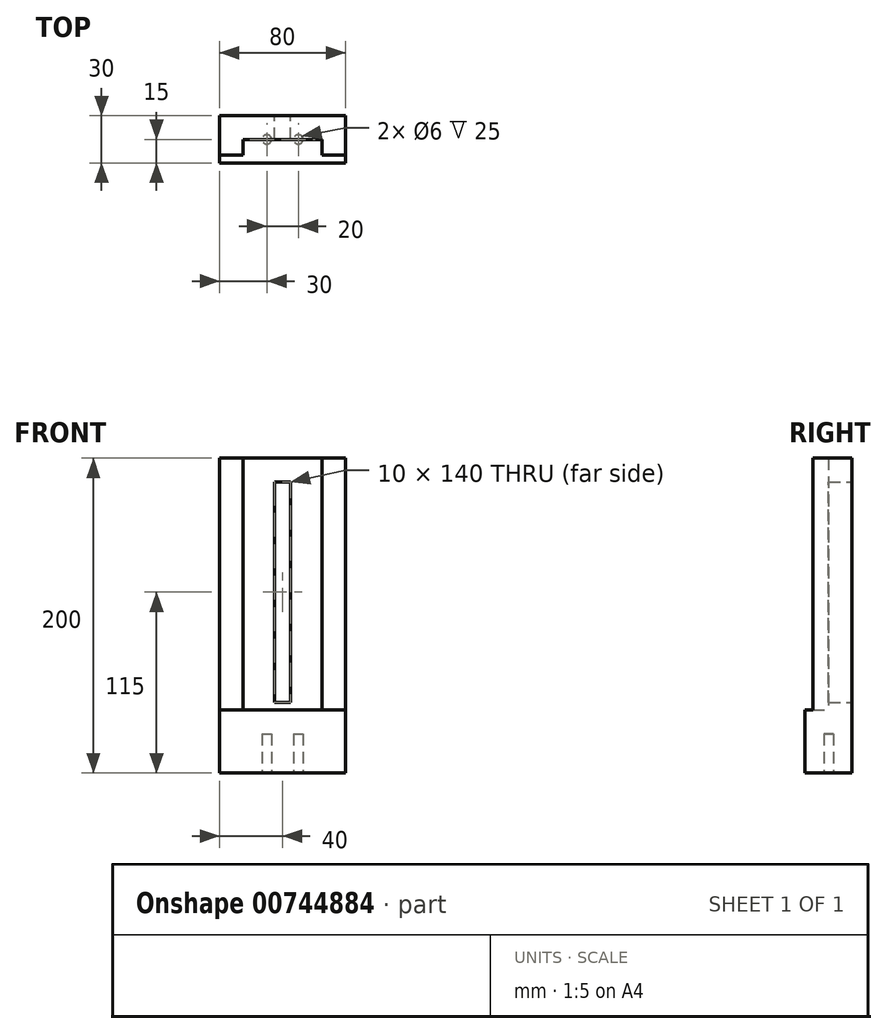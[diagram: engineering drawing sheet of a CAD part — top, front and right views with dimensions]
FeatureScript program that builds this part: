
annotation { "Feature Type Name" : "Feature", "Feature Type Description" : "" }
export const myFeature = defineFeature(function(context is Context, id is Id, definition is map)
    precondition{}
    {
        {
            var Q0;
            Q0=qCreatedBy(makeId("Front.planeOp"),FACE);
            var sketch = newSketch(context, id + "F0", { "sketchPlane" : qUnion([Q0])});
            skLineSegment(sketch, "E0.bottom", {"start": v(40, -100) * mm, "end": v(-40, -100) * mm});
            skLineSegment(sketch, "E0.top", {"start": v(40, 100) * mm, "end": v(-40, 100) * mm});
            skLineSegment(sketch, "E0.left", {"start": v(40, -100) * mm, "end": v(40, 100) * mm});
            skLineSegment(sketch, "E0.right", {"start": v(-40, -100) * mm, "end": v(-40, 100) * mm});
            skPoint(sketch, "E0.middle", {"position": v(0, 0) * mm});
            skLineSegment(sketch, "E1", {"start": v(-40, -60) * mm, "end": v(40, -60) * mm});
            skLineSegment(sketch, "E2", {"start": v(-25, 100) * mm, "end": v(-25, -60) * mm});
            skLineSegment(sketch, "E3.MirrorCS", {"start": v(25, 100) * mm, "end": v(25, -60) * mm});
            skLineSegment(sketch, "E4.bottom", {"start": v(5, -55) * mm, "end": v(-5, -55) * mm});
            skLineSegment(sketch, "E4.top", {"start": v(5, 85) * mm, "end": v(-5, 85) * mm});
            skLineSegment(sketch, "E4.left", {"start": v(5, -55) * mm, "end": v(5, 85) * mm});
            skLineSegment(sketch, "E4.right", {"start": v(-5, -55) * mm, "end": v(-5, 85) * mm});
            skPoint(sketch, "E4.middle", {"position": v(0, 15) * mm});
            skSolve(sketch);
        }
        {
            var Q0;
            {var subQ0=sQuery(id+"F0.wireOp",EDGE,"E2");Q0=makeQuery(id+"F0.imprint","IMPRINT",FACE,{"disambiguationData":[TD([[makeQuery(id+"F0.imprint","IMPRINT",EDGE,{"derivedFrom":subQ0}),1.0]])]});}
            extrude(context, id + "F1", {"entities" : qUnion([Q0]), "depth" : 15 * mm, "offsetDistance" : 25 * mm});
        }
        {
            var Q0;
            {var subQ4=sQuery(id+"F0.wireOp",EDGE,"E0.bottom");Q0=makeQuery(id+"F0.imprint","IMPRINT",FACE,{"disambiguationData":[TD([[makeQuery(id+"F0.imprint","IMPRINT",EDGE,{"derivedFrom":subQ4}),-1.0]])]});}
            extrude(context, id + "F2", {"entities" : qUnion([Q0]), "operationType" : NewBodyOperationType.ADD, "depth" : 30 * mm, "offsetDistance" : 25 * mm});
        }
        {
            var Q0;
            Q0=makeQuery(id+"F2.opExtrude","SWEPT_FACE",FACE,{"disambiguationData":[OSD([sQuery(id+"F0.wireOp",EDGE,"E0.bottom")])]});
            var sketch = newSketch(context, id + "F3", { "sketchPlane" : qUnion([Q0])});
            skCircle(sketch, "E5", {"center": v(-10, 15) * mm, "radius": 3 * mm});
            skPoint(sketch, "E5.centerSnap0", {"position": v(-40, 15) * mm});
            skCircle(sketch, "E6.MirrorC", {"center": v(10, 15) * mm, "radius": 3 * mm});
            skSolve(sketch);
        }
        {
            var Q0;
            Q0 = qSketchRegion(id + "F3", true);
            extrude(context, id + "F4", {"entities" : qUnion([Q0]), "operationType" : NewBodyOperationType.REMOVE, "oppositeDirection" : true, "depth" : 25 * mm, "offsetDistance" : 25 * mm});
        }
        {
            var Q0;
            {var subQ3=sQuery(id+"F0.wireOp",EDGE,"E2");Q0=makeQuery(id+"F0.imprint","IMPRINT",FACE,{"disambiguationData":[TD([[makeQuery(id+"F0.imprint","IMPRINT",EDGE,{"derivedFrom":subQ3}),-1.0]])]});}
            var Q1;
            {var subQ3=sQuery(id+"F0.wireOp",EDGE,"E3.MirrorCS");Q1=makeQuery(id+"F0.imprint","IMPRINT",FACE,{"disambiguationData":[TD([[makeQuery(id+"F0.imprint","IMPRINT",EDGE,{"derivedFrom":subQ3}),1.0]])]});}
            extrude(context, id + "F5", {"entities" : qUnion([Q0, Q1]), "operationType" : NewBodyOperationType.ADD, "depth" : 25 * mm, "offsetDistance" : 25 * mm});
        }
    });
